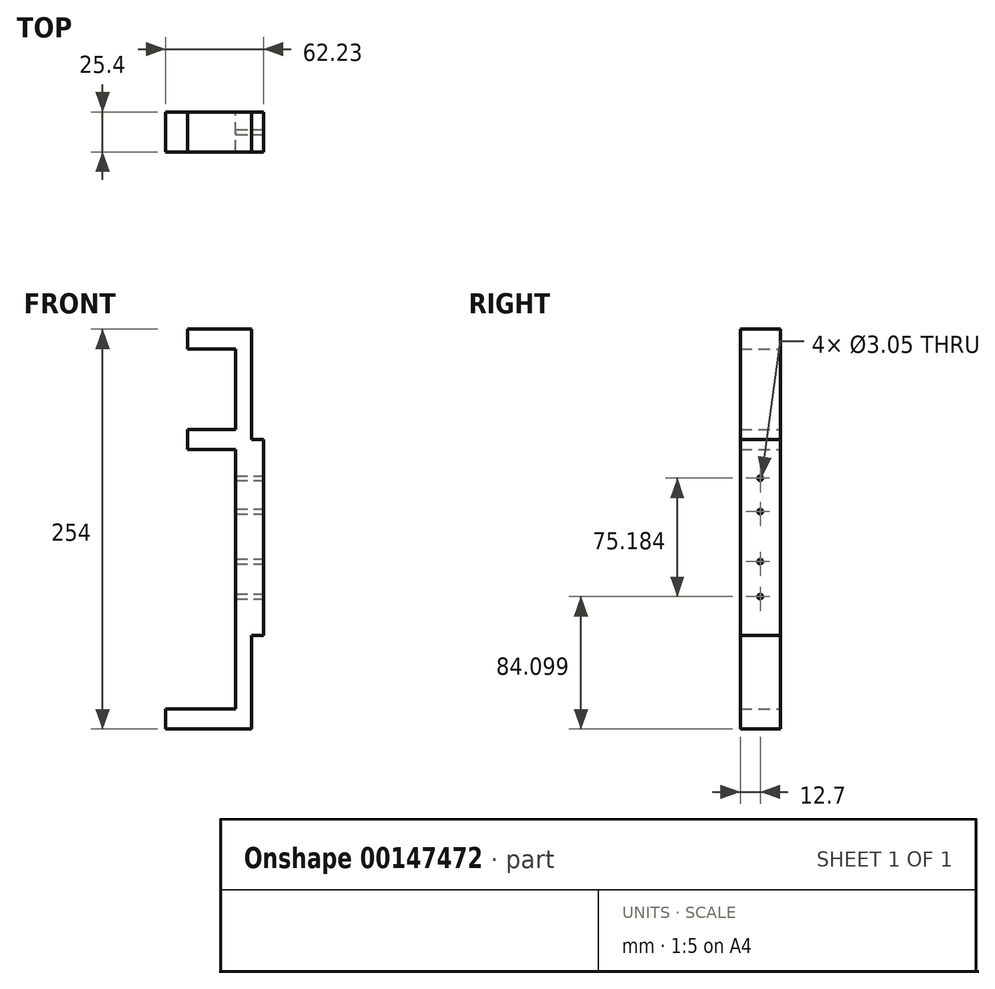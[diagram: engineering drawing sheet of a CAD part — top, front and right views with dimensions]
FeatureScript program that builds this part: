
annotation { "Feature Type Name" : "Feature", "Feature Type Description" : "" }
export const myFeature = defineFeature(function(context is Context, id is Id, definition is map)
    precondition{}
    {
        {
            var Q0;
            Q0=qCreatedBy(makeId("Front.planeOp"),FACE);
            var sketch = newSketch(context, id + "F0", { "sketchPlane" : qUnion([Q0])});
            skLineSegment(sketch, "E0.bottom", {"start": v(5.08, -127) * mm, "end": v(-5.08, -127) * mm});
            skLineSegment(sketch, "E0.top", {"start": v(5.08, 127) * mm, "end": v(-5.08, 127) * mm});
            skLineSegment(sketch, "E0.left", {"start": v(5.08, -127) * mm, "end": v(5.08, 127) * mm});
            skLineSegment(sketch, "E0.right", {"start": v(-5.08, -127) * mm, "end": v(-5.08, 127) * mm});
            skPoint(sketch, "E0.middle", {"position": v(0, 0) * mm});
            skLineSegment(sketch, "E1.bottom", {"start": v(5.08, 127) * mm, "end": v(-35.56, 127) * mm});
            skLineSegment(sketch, "E1.top", {"start": v(5.08, 114.3) * mm, "end": v(-35.56, 114.3) * mm});
            skLineSegment(sketch, "E1.left", {"start": v(5.08, 127) * mm, "end": v(5.08, 114.3) * mm});
            skLineSegment(sketch, "E1.right", {"start": v(-35.56, 127) * mm, "end": v(-35.56, 114.3) * mm});
            skLineSegment(sketch, "E2.bottom", {"start": v(5.08, 63.12) * mm, "end": v(-35.56, 63.12) * mm});
            skLineSegment(sketch, "E2.top", {"start": v(5.08, 50.42) * mm, "end": v(-35.56, 50.42) * mm});
            skLineSegment(sketch, "E2.left", {"start": v(5.08, 63.12) * mm, "end": v(5.08, 50.42) * mm});
            skLineSegment(sketch, "E2.right", {"start": v(-35.56, 63.12) * mm, "end": v(-35.56, 50.42) * mm});
            skLineSegment(sketch, "E3.bottom", {"start": v(-5.08, -127) * mm, "end": v(-49.53, -127) * mm});
            skLineSegment(sketch, "E3.top", {"start": v(-5.08, -114.3) * mm, "end": v(-49.53, -114.3) * mm});
            skLineSegment(sketch, "E3.left", {"start": v(-5.08, -127) * mm, "end": v(-5.08, -114.3) * mm});
            skLineSegment(sketch, "E3.right", {"start": v(-49.53, -127) * mm, "end": v(-49.53, -114.3) * mm});
            skLineSegment(sketch, "E4.bottom", {"start": v(5.08, 56.77) * mm, "end": v(12.7, 56.77) * mm});
            skLineSegment(sketch, "E4.top", {"start": v(5.08, -67.7) * mm, "end": v(12.7, -67.7) * mm});
            skLineSegment(sketch, "E4.left", {"start": v(5.08, 56.77) * mm, "end": v(5.08, -67.7) * mm});
            skLineSegment(sketch, "E4.right", {"start": v(12.7, 56.77) * mm, "end": v(12.7, -67.7) * mm});
            skSolve(sketch);
        }
        {
            var Q0;
            Q0=qSketchRegion(id+"F0",true);
            var Q1;
            {var subQ5=sQuery(id+"F0.wireOp",EDGE,"E1.right");Q1=makeQuery(id+"F0.imprint","IMPRINT",FACE,{"disambiguationData":[TD([[makeQuery(id+"F0.imprint","IMPRINT",EDGE,{"derivedFrom":subQ5}),1.0]])]});}
            extrude(context, id + "F1", {"entities" : qUnion([Q0, Q1]), "endBound" : BoundingType.SYMMETRIC, "depth" : 25.4 * mm});
        }
        {
            var Q0;
            Q0=makeQuery(id+"F1.opExtrude","SWEPT_FACE",FACE,{"disambiguationData":[OSD([sQuery(id+"F0.wireOp",EDGE,"E4.right")])]});
            var sketch = newSketch(context, id + "F2", { "sketchPlane" : qUnion([Q0])});
            skCircle(sketch, "E5", {"center": v(0, 32.28) * mm, "radius": 1.52 * mm});
            skCircle(sketch, "E6", {"center": v(0, -42.9) * mm, "radius": 1.52 * mm});
            skCircle(sketch, "E7", {"center": v(0, 11.07) * mm, "radius": 1.52 * mm});
            skCircle(sketch, "E8", {"center": v(0, -20.68) * mm, "radius": 1.52 * mm});
            skLineSegment(sketch, "E9", {"start": v(-12.7, -4.8) * mm, "end": v(12.7, -4.8) * mm, "construction": true});
            skSolve(sketch);
        }
        {
            var Q0;
            Q0=makeQuery(id+"F2.imprint","IMPRINT",FACE,{"disambiguationData":[TD([[makeQuery(id+"F2.imprint","IMPRINT",EDGE,{"derivedFrom":sQuery(id+"F2.wireOp",EDGE,"E5")}),1.0]])]});
            var Q1;
            Q1=makeQuery(id+"F2.imprint","IMPRINT",FACE,{"disambiguationData":[TD([[makeQuery(id+"F2.imprint","IMPRINT",EDGE,{"derivedFrom":sQuery(id+"F2.wireOp",EDGE,"E7")}),1.0]])]});
            var Q2;
            Q2=makeQuery(id+"F2.imprint","IMPRINT",FACE,{"disambiguationData":[TD([[makeQuery(id+"F2.imprint","IMPRINT",EDGE,{"derivedFrom":sQuery(id+"F2.wireOp",EDGE,"E8")}),1.0]])]});
            var Q3;
            Q3=makeQuery(id+"F2.imprint","IMPRINT",FACE,{"disambiguationData":[TD([[makeQuery(id+"F2.imprint","IMPRINT",EDGE,{"derivedFrom":sQuery(id+"F2.wireOp",EDGE,"E6")}),1.0]])]});
            extrude(context, id + "F3", {"entities" : qUnion([Q0, Q1, Q2, Q3]), "operationType" : NewBodyOperationType.REMOVE, "oppositeDirection" : true, "depth" : 25.4 * mm});
        }
    });
